# Revit family: NLRS_90_SI_Fietsenrek-Falco_Eco_Enkelzijdig_flc_FLC
name_source: partatom
category: Specialty Equipment
units: mm (PartAtom-declared; Revit-internal decimal feet)

## family parameters
Always vertical = Yes
Cut with Voids When Loaded = No
Enable Cutting in Views = No
Maintain Annotation Orientation = No
OmniClass Number = 23.40.10.11.11
OmniClass Title = Bicycle Racks
Part Type = Normal
Room Calculation Point = No
Round Connector Dimension = Use Diameter
Shared = Yes
Work Plane-Based = No

## types (19) — shared parameters
Assembly Code = 90.71
ClassificationCode = 90.71
NLRS_C_leverancier_bedrijfsnaam = Falco BV
NLRS_C_leverancier_url = https://www.falco.nl
NLRS_C_omschrijving = FalcoLevel Eco Cycle Rack
NLRS_C_uitvoering = Single sided
zero-valued in all types: Default Elevation

## per-type parameters (varying)
| type | FAL_afstand | FAL_afstand_P1 | FAL_afstand_P2 | FAL_afstand_P3 | FAL_afstand_P4 | FAL_afstand_P5 | FAL_afstand_P6 | FAL_afstand_P7 | FAL_afstand_P8 | FAL_array_1 | FAL_array_2 | NLRS_C_aantal | NLRS_C_hartafstand | NLRS_C_leverancier_artikel_code |
| FalcoLevel Eco ss ctc 400 8+8 | 43 mm | 96 mm  [stored 0.314961 ft] | 296 mm | 496 mm | 696 mm | 896 mm | 1096 mm  [stored 3.5958 ft] | 1296 mm | 1496 mm | 4 | 4 | 16 | 400 mm | 00.308.040 |
| FalcoLevel Eco ss ctc 400 7+7 | 43 mm | 96 mm  [stored 0.314961 ft] | 296 mm | 496 mm | 696 mm | 896 mm | 1096 mm  [stored 3.5958 ft] | 1296 mm | 1496 mm | 4 | 3 | 14 | 400 mm | 00.307.040 |
| FalcoLevel Eco ss ctc 400 6+6 | 43 mm | 96 mm  [stored 0.314961 ft] | 296 mm | 496 mm | 696 mm | 896 mm | 1096 mm  [stored 3.5958 ft] | 1296 mm | 1496 mm | 3 | 3 | 12 | 400 mm | 00.306.040 |
| FalcoLevel Eco ss ctc 400 5+5 | 43 mm | 96 mm  [stored 0.314961 ft] | 296 mm | 496 mm | 696 mm | 896 mm | 1096 mm  [stored 3.5958 ft] | 1296 mm | 1496 mm | 3 | 2 | 10 | 400 mm | 00.305.040 |
| FalcoLevel Eco ss ctc 400 4+4 | 43 mm | 96 mm  [stored 0.314961 ft] | 296 mm | 496 mm | 696 mm | 896 mm | 1096 mm  [stored 3.5958 ft] | 1296 mm | 1496 mm | 2 | 2 | 8 | 400 mm | 00.304.040 |
| FalcoLevel Eco ss ctc 400 3+3 | 43 mm | 96 mm  [stored 0.314961 ft] | 296 mm | 496 mm | 696 mm | 896 mm | 1096 mm  [stored 3.5958 ft] | 1296 mm | 1496 mm | 2 | 2 | 6 | 400 mm | 00.303.040 |
| FalcoLevel Eco ss ctc 400 2+2 | 43 mm | 96 mm  [stored 0.314961 ft] | 296 mm | 496 mm | 696 mm | 896 mm | 1096 mm  [stored 3.5958 ft] | 1296 mm | 1496 mm | 2 | 2 | 4 | 400 mm | 00.302.040 |
| FalcoLevel Eco ss ctc 375 2+2 | 55 mm | 96 mm  [stored 0.314961 ft] | 284 mm | 471 mm | 659 mm | 846 mm | 1034 mm  [stored 3.39239 ft] | 1221 mm | 1409 mm | 2 | 2 | 4 | 375 mm | 00.302.037 |
| FalcoLevel Eco ss ctc 375 3+3 | 55 mm | 96 mm  [stored 0.314961 ft] | 284 mm | 471 mm | 659 mm | 846 mm | 1034 mm  [stored 3.39239 ft] | 1221 mm | 1409 mm | 2 | 2 | 6 | 375 mm | 00.303.037 |
| FalcoLevel Eco ss ctc 375 4+4 | 55 mm | 96 mm  [stored 0.314961 ft] | 284 mm | 471 mm | 659 mm | 846 mm | 1034 mm  [stored 3.39239 ft] | 1221 mm | 1409 mm | 2 | 2 | 8 | 375 mm | 00.304.037 |
| FalcoLevel Eco ss ctc 375 5+5 | 55 mm | 96 mm  [stored 0.314961 ft] | 284 mm | 471 mm | 659 mm | 846 mm | 1034 mm  [stored 3.39239 ft] | 1221 mm | 1409 mm | 3 | 2 | 10 | 375 mm | 00.305.037 |
| FalcoLevel Eco ss ctc 375 6+6 | 55 mm | 96 mm  [stored 0.314961 ft] | 284 mm | 471 mm | 659 mm | 846 mm | 1034 mm  [stored 3.39239 ft] | 1221 mm | 1409 mm | 3 | 3 | 12 | 375 mm | 00.306.037 |
| FalcoLevel Eco ss ctc 375 7+7 | 55 mm | 96 mm  [stored 0.314961 ft] | 284 mm | 471 mm | 659 mm | 846 mm | 1034 mm  [stored 3.39239 ft] | 1221 mm | 1409 mm | 4 | 3 | 14 | 375 mm | 00.307.037 |
| FalcoLevel Eco ss ctc 375 8+8 | 55 mm | 96 mm  [stored 0.314961 ft] | 284 mm | 471 mm | 659 mm | 846 mm | 1034 mm  [stored 3.39239 ft] | 1221 mm | 1409 mm | 4 | 4 | 16 | 375 mm | 00.308.037 |
| FalcoLevel Eco ss ctc 500 6+6 | 0 mm  [stored 0 ft] | 100 mm  [stored 0.328084 ft] | 350 mm  [stored 1.14829 ft] | 600 mm | 850 mm  [stored 2.78871 ft] | 1100 mm | 1350 mm | 1600 mm | 1850 mm | 3 | 3 | 12 | 500 mm  [stored 1.64042 ft] | 00.306.050 |
| FalcoLevel Eco ss ctc 500 5+5 | 0 mm  [stored 0 ft] | 100 mm  [stored 0.328084 ft] | 350 mm  [stored 1.14829 ft] | 600 mm | 850 mm  [stored 2.78871 ft] | 1100 mm | 1350 mm | 1600 mm | 1850 mm | 3 | 2 | 10 | 500 mm  [stored 1.64042 ft] | 00.305.050 |
| FalcoLevel Eco ss ctc 500 4+4 | 0 mm  [stored 0 ft] | 100 mm  [stored 0.328084 ft] | 350 mm  [stored 1.14829 ft] | 600 mm | 850 mm  [stored 2.78871 ft] | 1100 mm | 1350 mm | 1600 mm | 1850 mm | 2 | 2 | 8 | 500 mm  [stored 1.64042 ft] | 00.304.050 |
| FalcoLevel Eco ss ctc 500 3+3 | 0 mm  [stored 0 ft] | 100 mm  [stored 0.328084 ft] | 350 mm  [stored 1.14829 ft] | 600 mm | 850 mm  [stored 2.78871 ft] | 1100 mm | 1350 mm | 1600 mm | 1850 mm | 2 | 2 | 6 | 500 mm  [stored 1.64042 ft] | 00.303.050 |
| FalcoLevel Eco ss ctc 500 2+2 | 0 mm  [stored 0 ft] | 100 mm  [stored 0.328084 ft] | 350 mm  [stored 1.14829 ft] | 600 mm | 850 mm  [stored 2.78871 ft] | 1100 mm | 1350 mm | 1600 mm | 1850 mm | 2 | 2 | 4 | 500 mm  [stored 1.64042 ft] | 00.302.050 |

note: [stored X ft] marks values corroborated as IEEE doubles in the binary element streams (Revit-internal decimal feet)

## geometry (parser evidence)
native form markers: Sweep x16
no freeform markers — native parametric forms only
